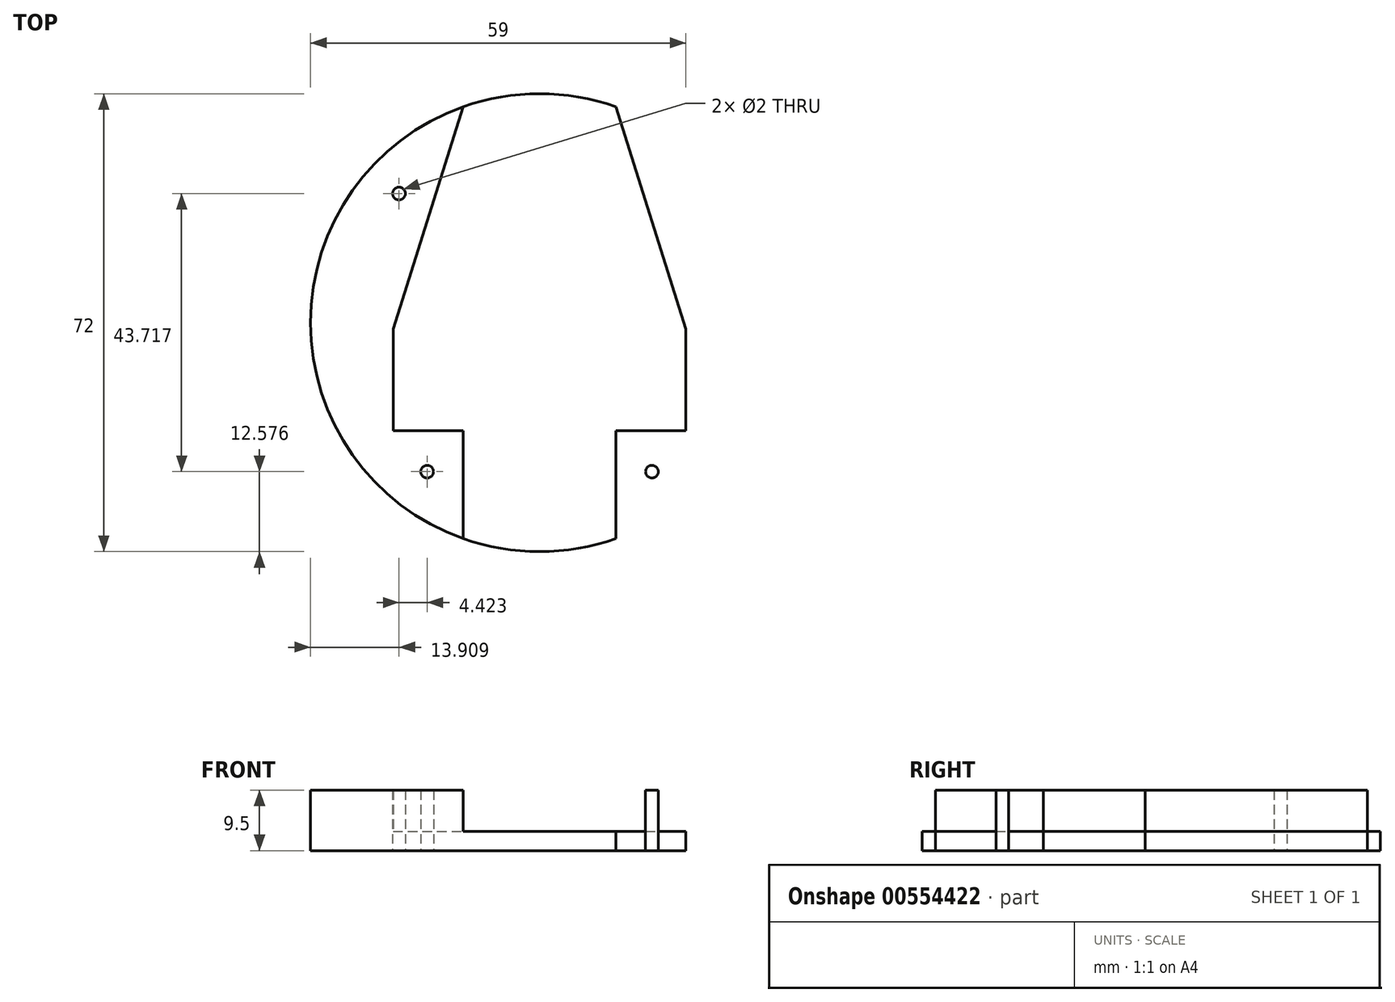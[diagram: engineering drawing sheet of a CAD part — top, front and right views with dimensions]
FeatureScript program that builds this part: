
annotation { "Feature Type Name" : "Feature", "Feature Type Description" : "" }
export const myFeature = defineFeature(function(context is Context, id is Id, definition is map)
    precondition{}
    {
        {
            var Q0;
            Q0=qCreatedBy(makeId("Top.planeOp"),FACE);
            var sketch = newSketch(context, id + "F0", { "sketchPlane" : qUnion([Q0])});
            skCircle(sketch, "E0", {"center": v(0, 0) * mm, "radius": 36 * mm});
            skLineSegment(sketch, "E1", {"start": v(0, 70.62) * mm, "end": v(0, -70.5) * mm, "construction": true});
            skLineSegment(sketch, "E2", {"start": v(-12, -33.94) * mm, "end": v(-12, -17) * mm});
            skLineSegment(sketch, "E3", {"start": v(-12, -17) * mm, "end": v(-23, -17) * mm});
            skLineSegment(sketch, "E4", {"start": v(-23, -17) * mm, "end": v(-23, -1) * mm});
            skPoint(sketch, "E5.orphan", {"position": v(-12, -40.47) * mm});
            skPoint(sketch, "E6.start.orphan", {"position": v(0, -36) * mm});
            skLineSegment(sketch, "E7", {"start": v(-12, 33.94) * mm, "end": v(-23, -1) * mm});
            skCircle(sketch, "E8", {"center": v(-22.1, 20.3) * mm, "radius": 1 * mm});
            skCircle(sketch, "E9", {"center": v(-17.67, -23.42) * mm, "radius": 1 * mm});
            skCircle(sketch, "E10.MirrorC", {"center": v(17.67, -23.42) * mm, "radius": 1 * mm});
            skLineSegment(sketch, "E11.MirrorCS", {"start": v(12, -33.94) * mm, "end": v(12, -17) * mm});
            skLineSegment(sketch, "E12.MirrorCS", {"start": v(12, -17) * mm, "end": v(23, -17) * mm});
            skLineSegment(sketch, "E13.MirrorCS", {"start": v(12, 33.94) * mm, "end": v(23, -1) * mm});
            skLineSegment(sketch, "E14.MirrorCS", {"start": v(23, -17) * mm, "end": v(23, -1) * mm});
            skCircle(sketch, "E15.MirrorC", {"center": v(22.1, 20.3) * mm, "radius": 1 * mm});
            skSolve(sketch);
        }
        {
            var Q0;
            {var subQ0=sQuery(id+"F0.wireOp",EDGE,"E2");Q0=makeQuery(id+"F0.imprint","IMPRINT",FACE,{"disambiguationData":[TD([[makeQuery(id+"F0.imprint","IMPRINT",EDGE,{"derivedFrom":subQ0}),1.0]])]});}
            var Q1;
            {var subQ0=sQuery(id+"F0.wireOp",EDGE,"E2");Q1=makeQuery(id+"F0.imprint","IMPRINT",FACE,{"disambiguationData":[TD([[makeQuery(id+"F0.imprint","IMPRINT",EDGE,{"derivedFrom":subQ0}),-1.0]])]});}
            var Q2;
            Q2=makeQuery(id+"F0.imprint","IMPRINT",FACE,{"disambiguationData":[TD([[makeQuery(id+"F0.imprint","IMPRINT",EDGE,{"derivedFrom":sQuery(id+"F0.wireOp",EDGE,"E10.MirrorC")}),1.0]])]});
            extrude(context, id + "F1", {"entities" : qUnion([Q0, Q1, Q2]), "depth" : 3 * mm, "offsetDistance" : 25 * mm});
        }
        {
            var Q0;
            {var subQ0=sQuery(id+"F0.wireOp",EDGE,"E2");Q0=makeQuery(id+"F0.imprint","IMPRINT",FACE,{"disambiguationData":[TD([[makeQuery(id+"F0.imprint","IMPRINT",EDGE,{"derivedFrom":subQ0}),1.0]])]});}
            var Q1;
            Q1=makeQuery(id+"F0.imprint","IMPRINT",FACE,{"disambiguationData":[TD([[makeQuery(id+"F0.imprint","IMPRINT",EDGE,{"derivedFrom":sQuery(id+"F0.wireOp",EDGE,"E10.MirrorC")}),1.0]])]});
            extrude(context, id + "F2", {"entities" : qUnion([Q0, Q1]), "operationType" : NewBodyOperationType.ADD, "depth" : 9.5 * mm, "offsetDistance" : 25 * mm});
        }
    });
